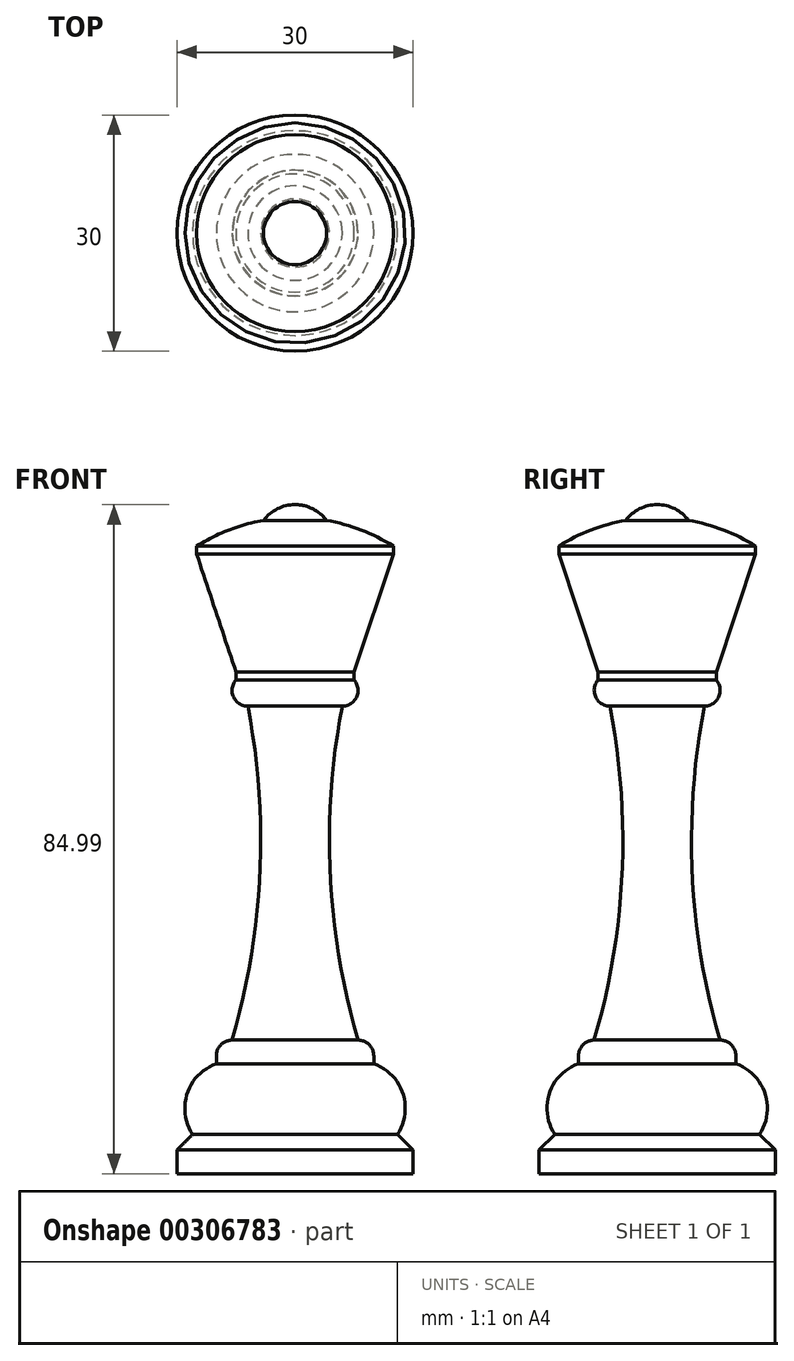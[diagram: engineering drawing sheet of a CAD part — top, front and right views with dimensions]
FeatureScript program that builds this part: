
annotation { "Feature Type Name" : "Feature", "Feature Type Description" : "" }
export const myFeature = defineFeature(function(context is Context, id is Id, definition is map)
    precondition{}
    {
        {
            var Q0;
            Q0=qCreatedBy(makeId("Front.planeOp"),FACE);
            var sketch = newSketch(context, id + "F0", { "sketchPlane" : qUnion([Q0])});
            skArc(sketch, "E0", {"start": v(4, -2) * mm, "mid": v(2.24, -0.53) * mm, "end": v(0, 0) * mm});
            skArc(sketch, "E1", {"start": v(12.5, -5.27) * mm, "mid": v(8.41, -3.22) * mm, "end": v(4, -2) * mm});
            skLineSegment(sketch, "E2", {"start": v(12.5, -5.27) * mm, "end": v(12.5, -6.27) * mm});
            skLineSegment(sketch, "E3", {"start": v(12.5, -6.27) * mm, "end": v(7.5, -21.27) * mm});
            skLineSegment(sketch, "E4", {"start": v(7.5, -21.27) * mm, "end": v(7.5, -22.27) * mm});
            skArc(sketch, "E5", {"start": v(6, -25.6) * mm, "mid": v(7.82, -24.42) * mm, "end": v(7.5, -22.27) * mm});
            skLineSegment(sketch, "E6", {"start": v(10, -70.02) * mm, "end": v(10, -71.02) * mm});
            skArc(sketch, "E7", {"start": v(13, -80) * mm, "mid": v(13.7, -74.78) * mm, "end": v(10, -71.02) * mm});
            skLineSegment(sketch, "E8", {"start": v(13, -80) * mm, "end": v(15, -82) * mm});
            skLineSegment(sketch, "E9", {"start": v(15, -82) * mm, "end": v(15, -85) * mm});
            skLineSegment(sketch, "E10", {"start": v(15, -85) * mm, "end": v(0, -85) * mm});
            skLineSegment(sketch, "E11", {"start": v(0, -85) * mm, "end": v(0, 0) * mm});
            skArc(sketch, "E12", {"start": v(6, -25.6) * mm, "mid": v(4.46, -46.93) * mm, "end": v(8, -68.02) * mm});
            skArc(sketch, "E13", {"start": v(10, -70.02) * mm, "mid": v(9.41, -68.6) * mm, "end": v(8, -68.02) * mm});
            skSolve(sketch);
        }
        {
            var Q0;
            Q0=makeQuery(id+"F0.imprint","IMPRINT",FACE,{"disambiguationData":[TD([[makeQuery(id+"F0.imprint","IMPRINT",EDGE,{"derivedFrom":sQuery(id+"F0.wireOp",EDGE,"E0")}),1.0]])]});
            var Q1;
            Q1=sQuery(id+"F0.wireOp",EDGE,"E11");
            revolve(context, id + "F1", {"entities" : qUnion([Q0]), "axis" : qUnion([Q1]), "revolveType" : RevolveType.FULL});
        }
    });
